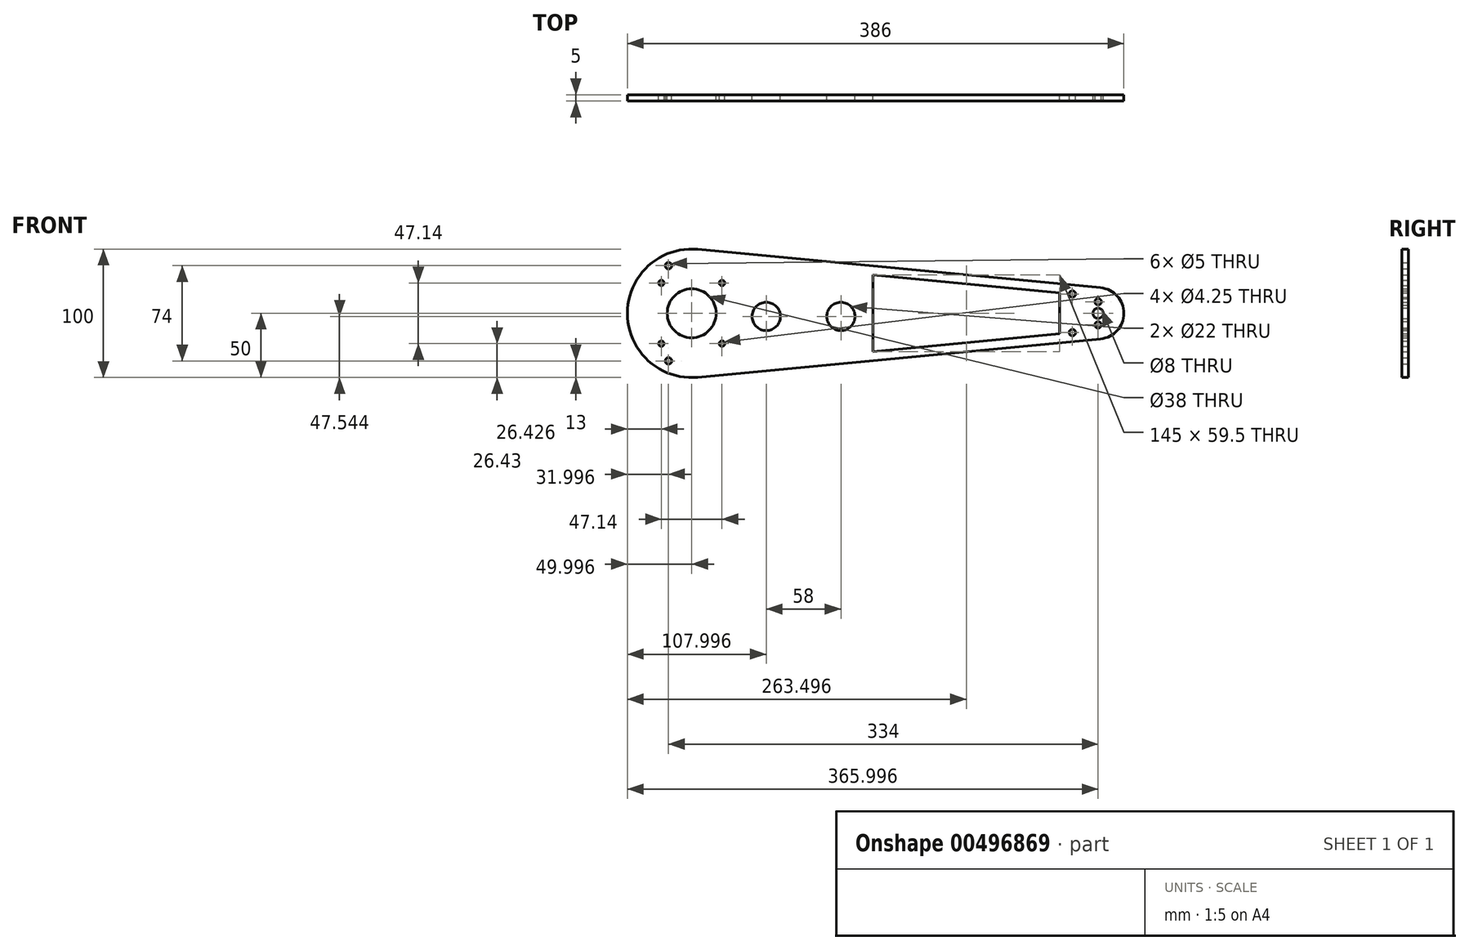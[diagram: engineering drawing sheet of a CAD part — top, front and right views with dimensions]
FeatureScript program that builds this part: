
annotation { "Feature Type Name" : "Feature", "Feature Type Description" : "" }
export const myFeature = defineFeature(function(context is Context, id is Id, definition is map)
    precondition{}
    {
        {
            var Q0;
            Q0=qCreatedBy(makeId("Front.planeOp"),FACE);
            var sketch = newSketch(context, id + "F0", { "sketchPlane" : qUnion([Q0])});
            skArc(sketch, "E0", {"start": v(-119.7, 49.77) * mm, "mid": v(-174.45, 0) * mm, "end": v(-119.7, -49.77) * mm});
            skCircle(sketch, "E1", {"center": v(-66.45, -2.46) * mm, "radius": 11 * mm});
            skCircle(sketch, "E2", {"center": v(-8.45, -2.46) * mm, "radius": 11 * mm});
            skCircle(sketch, "E3", {"center": v(-148.02, 23.57) * mm, "radius": 2.12 * mm});
            skCircle(sketch, "E4", {"center": v(-100.88, 23.57) * mm, "radius": 2.12 * mm});
            skCircle(sketch, "E5", {"center": v(-100.88, -23.57) * mm, "radius": 2.12 * mm});
            skCircle(sketch, "E6", {"center": v(-148.02, -23.57) * mm, "radius": 2.12 * mm});
            skCircle(sketch, "E7", {"center": v(-124.45, 0) * mm, "radius": 19 * mm});
            skCircle(sketch, "E8", {"center": v(191.55, 0) * mm, "radius": 4 * mm});
            skArc(sketch, "E9", {"start": v(193.44, -19.9) * mm, "mid": v(211.55, 0) * mm, "end": v(193.44, 19.9) * mm});
            skLineSegment(sketch, "E10", {"start": v(-119.7, 49.77) * mm, "end": v(193.44, 19.9) * mm});
            skLineSegment(sketch, "E11", {"start": v(-119.7, -49.77) * mm, "end": v(193.44, -19.9) * mm});
            skCircle(sketch, "E12", {"center": v(-142.45, 37) * mm, "radius": 2.5 * mm});
            skCircle(sketch, "E13", {"center": v(-142.45, -37) * mm, "radius": 2.5 * mm});
            skCircle(sketch, "E14", {"center": v(171.55, 15) * mm, "radius": 2.5 * mm});
            skCircle(sketch, "E15", {"center": v(171.55, -15) * mm, "radius": 2.5 * mm});
            skLineSegment(sketch, "E16", {"start": v(191.55, 0) * mm, "end": v(191.55, 9) * mm});
            skLineSegment(sketch, "E17", {"start": v(191.55, 0) * mm, "end": v(191.55, -9) * mm});
            skCircle(sketch, "E18", {"center": v(191.55, 9) * mm, "radius": 2.5 * mm});
            skCircle(sketch, "E19", {"center": v(191.55, -9) * mm, "radius": 2.5 * mm});
            skLineSegment(sketch, "E20", {"start": v(16.55, 29.75) * mm, "end": v(161.55, 15.92) * mm});
            skLineSegment(sketch, "E21", {"start": v(161.55, 15.92) * mm, "end": v(161.55, -15.92) * mm});
            skLineSegment(sketch, "E22", {"start": v(161.55, -15.92) * mm, "end": v(16.55, -29.75) * mm});
            skLineSegment(sketch, "E23", {"start": v(16.55, -29.75) * mm, "end": v(16.55, 29.75) * mm});
            skSolve(sketch);
        }
        {
            var Q0;
            Q0 = qSketchRegion(id + "F0", true);
            extrude(context, id + "F1", {"entities" : qUnion([Q0]), "depth" : 5 * mm});
        }
    });
